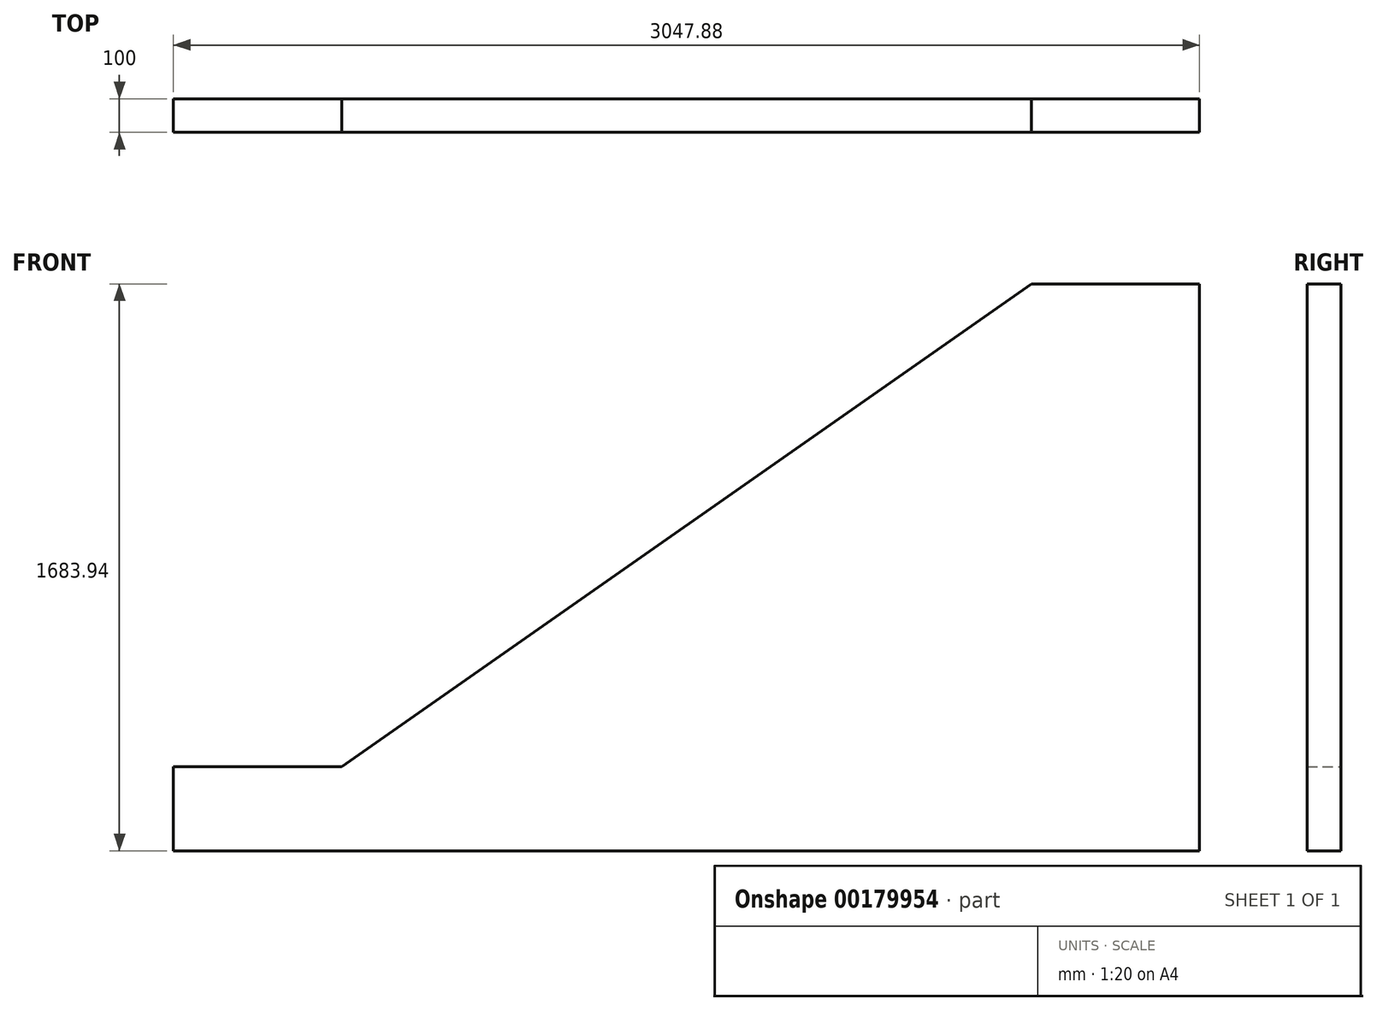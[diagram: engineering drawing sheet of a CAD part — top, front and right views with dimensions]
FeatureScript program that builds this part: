
annotation { "Feature Type Name" : "Feature", "Feature Type Description" : "" }
export const myFeature = defineFeature(function(context is Context, id is Id, definition is map)
    precondition{}
    {
        {
            var Q0;
            Q0=qCreatedBy(makeId("Front.planeOp"),FACE);
            var sketch = newSketch(context, id + "F0", { "sketchPlane" : qUnion([Q0])});
            skLineSegment(sketch, "E0", {"start": v(0, 0) * mm, "end": v(500, 0) * mm});
            skLineSegment(sketch, "E1", {"start": v(500, 0) * mm, "end": v(2547.88, 1433.94) * mm});
            skLineSegment(sketch, "E2", {"start": v(2547.88, 1433.94) * mm, "end": v(3047.88, 1433.94) * mm});
            skLineSegment(sketch, "E3", {"start": v(0, 0) * mm, "end": v(0, -250) * mm});
            skLineSegment(sketch, "E4", {"start": v(0, -250) * mm, "end": v(3047.88, -250) * mm});
            skLineSegment(sketch, "E5", {"start": v(3047.88, -250) * mm, "end": v(3047.88, 1433.94) * mm});
            skSolve(sketch);
        }
        {
            var Q0;
            Q0=qSketchRegion(id+"F0",true);
            extrude(context, id + "F1", {"entities" : qUnion([Q0]), "depth" : 100 * mm});
        }
    });
